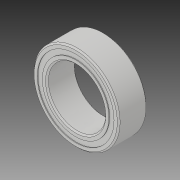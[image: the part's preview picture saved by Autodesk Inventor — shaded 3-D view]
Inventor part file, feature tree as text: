
AUTODESK INVENTOR PART (.ipt)
format: ipt  version: 2019 (Build 230136000, 136)  size: 586,240 bytes
history: native  units: in
note: dims shown in document units (in); Inventor stores cm internally (conversion verified against a paired STEP export)
features: other x11, revolve x5
ambient origin geometry x8: Origin, YZ Plane, XZ Plane, XY Plane, X Axis, Y Axis, Z Axis, Center Point
bodies: Solid1 (feature_tree), Solid2 (feature_tree), Solid3 (feature_tree), Solid4 (feature_tree), Solid5 (feature_tree), Solid6 (feature_tree), Solid7 (feature_tree), Solid8 (feature_tree), Solid9 (feature_tree), Solid10 (feature_tree), Solid11 (feature_tree), Solid12 (feature_tree), Solid13 (feature_tree), Solid14 (feature_tree), Solid15 (feature_tree), Solid16 (feature_tree)
feature tree (16):
  revolve  "Revolve1"  [1 undecoded]
  revolve  "Revolve3"  [1 undecoded]
  revolve  "Revolve4"  [1 undecoded]
  other  "CirPattern1[1]"
  other  "CirPattern1[2]"
  other  "CirPattern1[3]"
  other  "CirPattern1[4]"
  other  "CirPattern1[5]"
  other  "CirPattern1[6]"
  other  "CirPattern1[7]"
  other  "CirPattern1[8]"
  other  "CirPattern1[9]"
  other  "CirPattern1[10]"
  other  "CirPattern1[11]"
  revolve  "Revolve5[1]"  [1 undecoded]
  revolve  "Revolve5[2]"  [1 undecoded]
note: 5 required parameter values undecoded (feature->parameter linkage not recoverable at this tier; creation-order binding heuristic only, values carry confidence <= 0.55)
